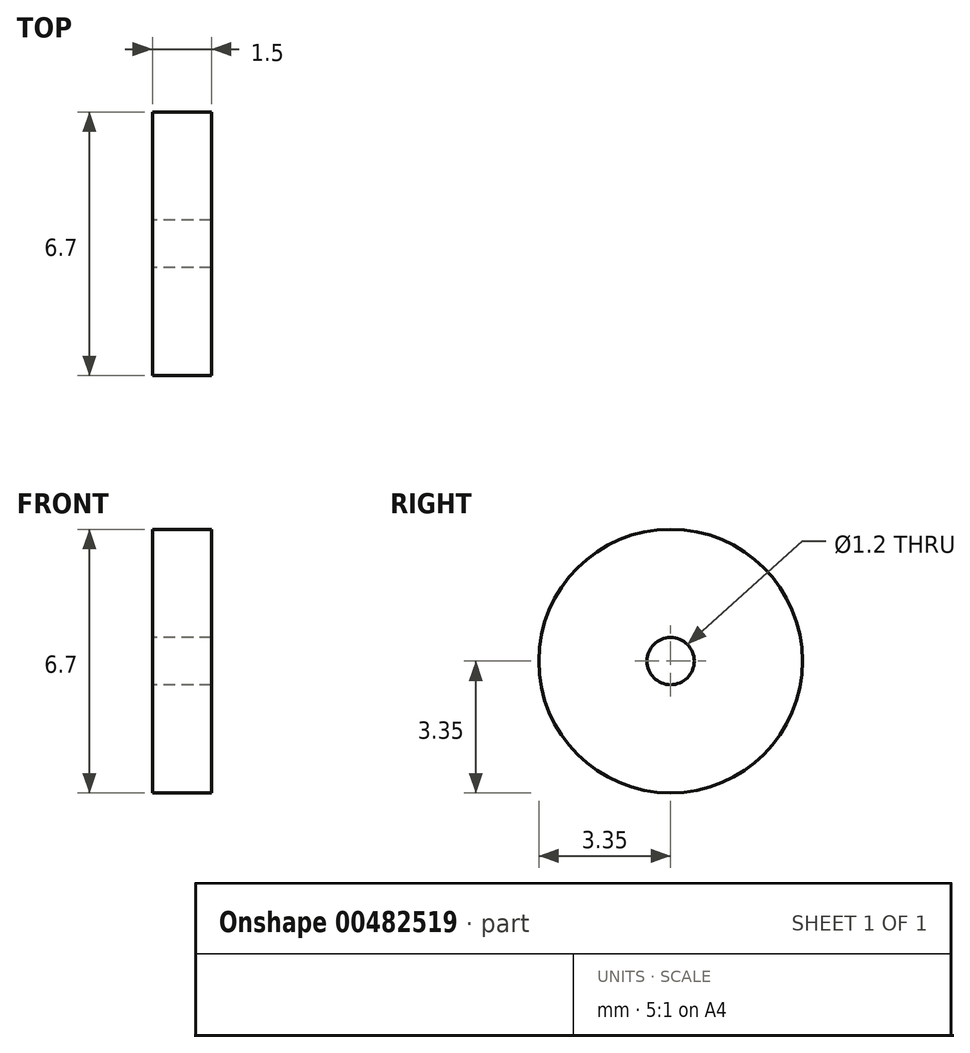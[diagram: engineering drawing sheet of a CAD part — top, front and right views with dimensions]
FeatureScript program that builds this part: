
annotation { "Feature Type Name" : "Feature", "Feature Type Description" : "" }
export const myFeature = defineFeature(function(context is Context, id is Id, definition is map)
    precondition{}
    {
        {
            var Q0;
            Q0=qCreatedBy(makeId("Top.planeOp"),FACE);
            var sketch = newSketch(context, id + "F0", { "sketchPlane" : qUnion([Q0])});
            skLineSegment(sketch, "E0.bottom", {"start": v(0, 0) * mm, "end": v(1.5, 0) * mm});
            skLineSegment(sketch, "E0.top", {"start": v(0, 3.35) * mm, "end": v(1.5, 3.35) * mm});
            skLineSegment(sketch, "E1", {"start": v(0, 3.35) * mm, "end": v(0, 0.6) * mm});
            skLineSegment(sketch, "E2", {"start": v(1.5, 3.35) * mm, "end": v(1.5, 0.6) * mm});
            skLineSegment(sketch, "E3", {"start": v(0, 0.6) * mm, "end": v(1.5, 0.6) * mm});
            skSolve(sketch);
        }
        {
            var Q0;
            Q0=makeQuery(id+"F0.imprint","IMPRINT",FACE,{"disambiguationData":[TD([[makeQuery(id+"F0.imprint","IMPRINT",EDGE,{"derivedFrom":sQuery(id+"F0.wireOp",EDGE,"E0.bottom")}),1.0]])]});
            var Q1;
            Q1=makeQuery(id+"F0.imprint","IMPRINT",FACE,{"disambiguationData":[TD([[makeQuery(id+"F0.imprint","IMPRINT",EDGE,{"derivedFrom":sQuery(id+"F0.wireOp",EDGE,"E0.top")}),-1.0]])]});
            var Q2;
            Q2=sQuery(id+"F0.wireOp",EDGE,"E0.bottom");
            revolve(context, id + "F1", {"entities" : qUnion([Q0, Q1]), "axis" : qUnion([Q2]), "revolveType" : RevolveType.FULL});
        }
    });
